# Revit family: Арабский вазон
name_source: partatom
category: Антураж
revit_build: Autodesk Revit 2017 (Build: 20160225_1515(x64)
units: mm (PartAtom-declared; Revit-internal decimal feet)

## family parameters
Всегда вертикально = Да
Источник визуального образа = Геометрия семейства
На основе рабочей плоскости = Нет
Общий = Нет
При загрузке вырезать с полостями = Нет
Точка расчета площади = Нет

## types (4) — shared parameters
ADSK_Код изделия = 8425
ADSK_Наименование = Вазон «Арабский»

Вазон «Арабский»

Вазон «Арабский»

Вазон «Арабский»

Вазон «Арабский»

Вазон «Арабский»

Вазон «Арабский»

Вазон «Арабский»
URL = https://hobbyka.ru
АDSK_Материал вазона = Стеклопластиковый композит с гранитной крошкой
Изготовитель = ООО "Хоббика"
Материал_1 = Стеклопластиковый композит с гранитной крошкой_Зеленый
Материал_2 = Стеклопластиковый композит с гранитной крошкой_Красный
zero-valued in all types: Высота

## per-type parameters (varying)
| type | ADSK_Размер_Высота | ADSK_Размер_Диаметр | Большой | Малый | Средний | Средний  плюс | Стоимость |
| Большой | 1020 мм | 495 мм | Да | Нет | Нет | Нет | 23230 $ |
| Средний | 715 мм | 555 мм | Нет | Нет | Да | Нет | 18400 $ |
| Средний плюс | 680 мм | 495 мм | Нет | Нет | Нет | Да | 19780 $ |
| Малый | 420 мм | 490 мм | Нет | Да | Нет | Нет | 14145 $ |
